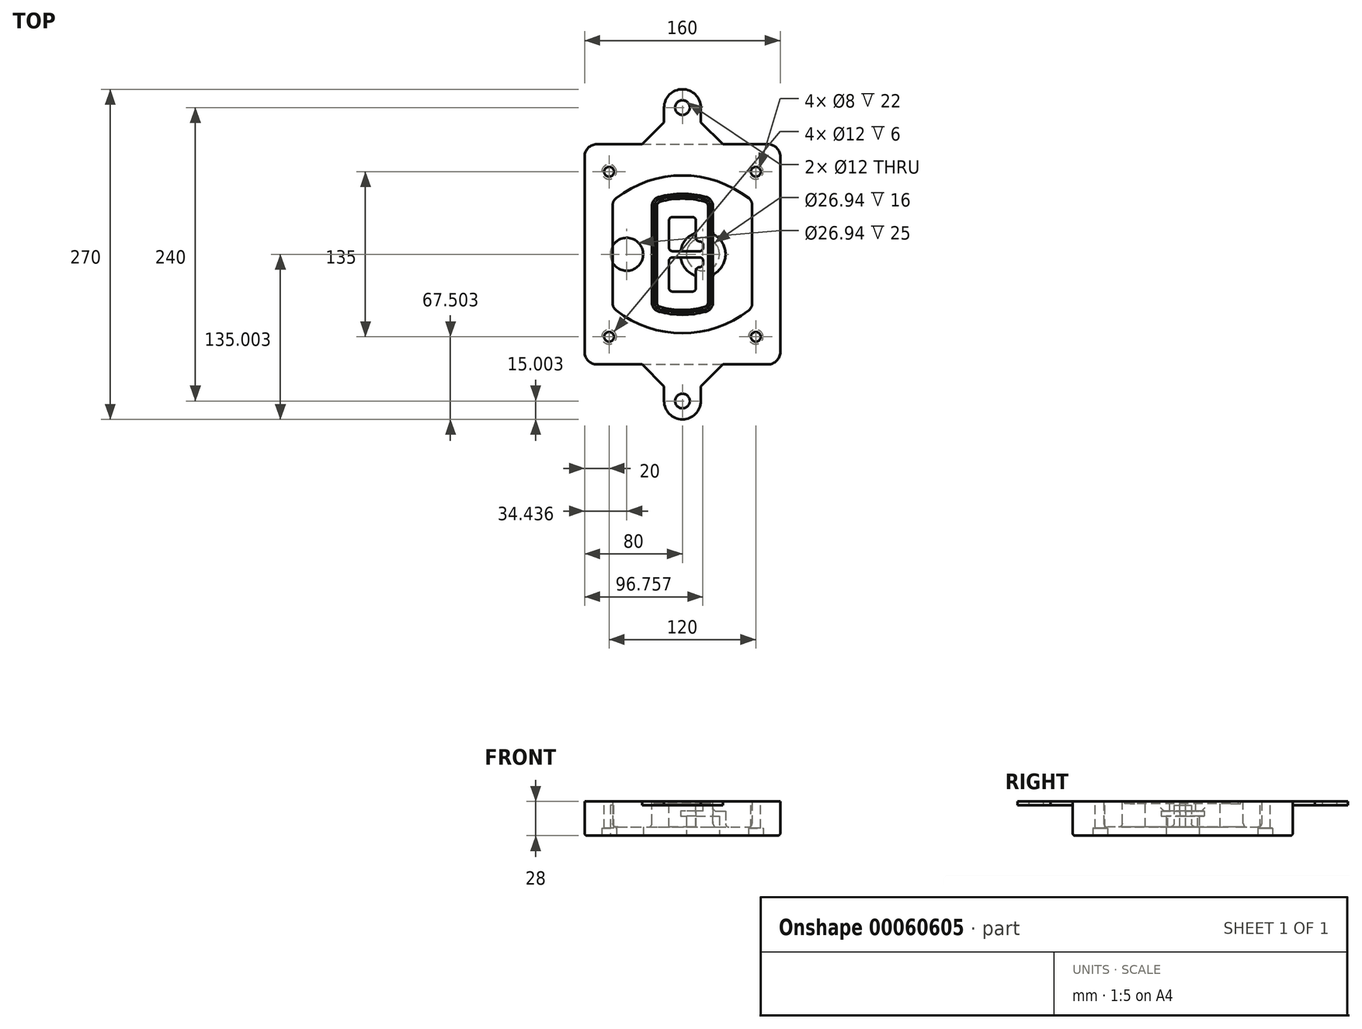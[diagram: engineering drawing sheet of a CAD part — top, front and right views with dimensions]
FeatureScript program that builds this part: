
annotation { "Feature Type Name" : "Feature", "Feature Type Description" : "" }
export const myFeature = defineFeature(function(context is Context, id is Id, definition is map)
    precondition{}
    {
        {
            var Q0;
            Q0=qCreatedBy(makeId("Top.planeOp"),FACE);
            var sketch = newSketch(context, id + "F0", { "sketchPlane" : qUnion([Q0])});
            skPoint(sketch, "E0.rect.middle", {"position": v(0, 0) * mm});
            skLineSegment(sketch, "E1.bottom", {"start": v(24.05, 28.38) * mm, "end": v(164.05, 28.38) * mm});
            skLineSegment(sketch, "E1.top", {"start": v(24.05, 208.38) * mm, "end": v(164.05, 208.38) * mm});
            skLineSegment(sketch, "E1.left", {"start": v(14.05, 38.38) * mm, "end": v(14.05, 198.38) * mm});
            skLineSegment(sketch, "E1.right", {"start": v(174.05, 38.38) * mm, "end": v(174.05, 198.38) * mm});
            skLineSegment(sketch, "E2", {"start": v(14.05, 208.38) * mm, "end": v(174.05, 28.38) * mm, "construction": true});
            skLineSegment(sketch, "E3", {"start": v(174.05, 208.38) * mm, "end": v(14.05, 28.38) * mm, "construction": true});
            skCircle(sketch, "E4", {"center": v(34.05, 185.88) * mm, "radius": 4 * mm});
            skCircle(sketch, "E5", {"center": v(154.05, 185.88) * mm, "radius": 4 * mm});
            skCircle(sketch, "E6", {"center": v(154.05, 50.88) * mm, "radius": 4 * mm});
            skCircle(sketch, "E7", {"center": v(34.05, 50.88) * mm, "radius": 4 * mm});
            skLineSegment(sketch, "E8", {"start": v(34.05, 185.88) * mm, "end": v(154.05, 185.88) * mm, "construction": true});
            skLineSegment(sketch, "E9", {"start": v(154.05, 185.88) * mm, "end": v(154.05, 50.88) * mm, "construction": true});
            skLineSegment(sketch, "E10", {"start": v(154.05, 50.88) * mm, "end": v(34.05, 50.88) * mm, "construction": true});
            skLineSegment(sketch, "E11", {"start": v(34.05, 50.88) * mm, "end": v(34.05, 185.88) * mm, "construction": true});
            skLineSegment(sketch, "E12", {"start": v(34.05, 158.68) * mm, "end": v(34.05, 78.09) * mm});
            skLineSegment(sketch, "E13", {"start": v(154.05, 158.68) * mm, "end": v(154.05, 78.09) * mm});
            skArc(sketch, "E14", {"start": v(150.2, 166.56) * mm, "mid": v(94.05, 185.88) * mm, "end": v(37.9, 166.56) * mm});
            skArc(sketch, "E15", {"start": v(37.9, 70.2) * mm, "mid": v(94.05, 50.88) * mm, "end": v(150.2, 70.2) * mm});
            skLineSegment(sketch, "E16", {"start": v(34.05, 118.38) * mm, "end": v(154.05, 118.38) * mm, "construction": true});
            skPoint(sketch, "E17.visualSharp", {"position": v(34.05, 73.38) * mm});
            skArc(sketch, "E17.filletArc", {"start": v(34.05, 78.09) * mm, "mid": v(35.06, 73.7) * mm, "end": v(37.9, 70.2) * mm});
            skPoint(sketch, "E18.visualSharp", {"position": v(34.05, 163.38) * mm});
            skArc(sketch, "E18.filletArc", {"start": v(37.9, 166.56) * mm, "mid": v(35.06, 163.06) * mm, "end": v(34.05, 158.68) * mm});
            skPoint(sketch, "E19.visualSharp", {"position": v(154.05, 163.38) * mm});
            skArc(sketch, "E19.filletArc", {"start": v(154.05, 158.68) * mm, "mid": v(153.04, 163.06) * mm, "end": v(150.2, 166.56) * mm});
            skPoint(sketch, "E20.visualSharp", {"position": v(154.05, 73.38) * mm});
            skArc(sketch, "E20.filletArc", {"start": v(150.2, 70.2) * mm, "mid": v(153.04, 73.7) * mm, "end": v(154.05, 78.09) * mm});
            skPoint(sketch, "E21.visualSharp", {"position": v(14.05, 208.38) * mm});
            skArc(sketch, "E21.filletArc", {"start": v(24.05, 208.38) * mm, "mid": v(16.98, 205.45) * mm, "end": v(14.05, 198.38) * mm});
            skPoint(sketch, "E22.visualSharp", {"position": v(174.05, 208.38) * mm});
            skArc(sketch, "E22.filletArc", {"start": v(174.05, 198.38) * mm, "mid": v(171.12, 205.45) * mm, "end": v(164.05, 208.38) * mm});
            skPoint(sketch, "E23.visualSharp", {"position": v(174.05, 28.38) * mm});
            skArc(sketch, "E23.filletArc", {"start": v(164.05, 28.38) * mm, "mid": v(171.12, 31.31) * mm, "end": v(174.05, 38.38) * mm});
            skPoint(sketch, "E24.visualSharp", {"position": v(14.05, 28.38) * mm});
            skArc(sketch, "E24.filletArc", {"start": v(14.05, 38.38) * mm, "mid": v(16.98, 31.31) * mm, "end": v(24.05, 28.38) * mm});
            skArc(sketch, "E25.0", {"start": v(151.05, 158.68) * mm, "mid": v(150.34, 161.75) * mm, "end": v(148.36, 164.2) * mm});
            skLineSegment(sketch, "E25.1", {"start": v(151.05, 158.68) * mm, "end": v(151.05, 78.09) * mm});
            skArc(sketch, "E25.2", {"start": v(148.36, 72.57) * mm, "mid": v(150.34, 75.02) * mm, "end": v(151.05, 78.09) * mm});
            skArc(sketch, "E25.3", {"start": v(39.74, 72.57) * mm, "mid": v(94.05, 53.88) * mm, "end": v(148.36, 72.57) * mm});
            skArc(sketch, "E25.4", {"start": v(37.05, 78.09) * mm, "mid": v(37.76, 75.02) * mm, "end": v(39.74, 72.57) * mm});
            skArc(sketch, "E25.5", {"start": v(148.36, 164.2) * mm, "mid": v(94.05, 182.88) * mm, "end": v(39.74, 164.2) * mm});
            skLineSegment(sketch, "E25.6", {"start": v(37.05, 158.68) * mm, "end": v(37.05, 78.09) * mm});
            skArc(sketch, "E25.7", {"start": v(39.74, 164.2) * mm, "mid": v(37.76, 161.75) * mm, "end": v(37.05, 158.68) * mm});
            skArc(sketch, "E26.0", {"start": v(35.43, 169.71) * mm, "mid": v(31.47, 164.82) * mm, "end": v(30.05, 158.68) * mm});
            skArc(sketch, "E26.1", {"start": v(152.67, 169.71) * mm, "mid": v(94.05, 189.88) * mm, "end": v(35.43, 169.71) * mm});
            skArc(sketch, "E26.2", {"start": v(158.05, 158.68) * mm, "mid": v(156.63, 164.82) * mm, "end": v(152.67, 169.71) * mm});
            skLineSegment(sketch, "E26.3", {"start": v(158.05, 158.68) * mm, "end": v(158.05, 78.09) * mm});
            skArc(sketch, "E26.4", {"start": v(152.67, 67.05) * mm, "mid": v(156.63, 71.95) * mm, "end": v(158.05, 78.09) * mm});
            skLineSegment(sketch, "E26.5", {"start": v(30.05, 158.68) * mm, "end": v(30.05, 78.09) * mm});
            skArc(sketch, "E26.6", {"start": v(35.43, 67.05) * mm, "mid": v(94.05, 46.88) * mm, "end": v(152.67, 67.05) * mm});
            skArc(sketch, "E26.7", {"start": v(30.05, 78.09) * mm, "mid": v(31.47, 71.95) * mm, "end": v(35.43, 67.05) * mm});
            skSolve(sketch);
        }
        {
            var Q0;
            Q0=makeQuery(id+"F0.imprint","IMPRINT",FACE,{"disambiguationData":[TD([[makeQuery(id+"F0.imprint","IMPRINT",EDGE,{"derivedFrom":sQuery(id+"F0.wireOp",EDGE,"E1.bottom")}),1.0]])]});
            var Q1;
            Q1=makeQuery(id+"F0.imprint","IMPRINT",FACE,{"disambiguationData":[TD([[makeQuery(id+"F0.imprint","IMPRINT",EDGE,{"derivedFrom":sQuery(id+"F0.wireOp",EDGE,"E12")}),1.0]])]});
            var Q2;
            Q2=makeQuery(id+"F0.imprint","IMPRINT",FACE,{"disambiguationData":[TD([[makeQuery(id+"F0.imprint","IMPRINT",EDGE,{"derivedFrom":sQuery(id+"F0.wireOp",EDGE,"E25.0")}),1.0]])]});
            var Q3;
            Q3=makeQuery(id+"F0.imprint","IMPRINT",FACE,{"disambiguationData":[TD([[makeQuery(id+"F0.imprint","IMPRINT",EDGE,{"derivedFrom":sQuery(id+"F0.wireOp",EDGE,"E12")}),-1.0]])]});
            extrude(context, id + "F1", {"entities" : qUnion([Q0, Q1, Q2, Q3]), "oppositeDirection" : true, "depth" : 25 * mm});
        }
        {
            var Q0;
            Q0=makeQuery(id+"F0.imprint","IMPRINT",FACE,{"disambiguationData":[TD([[makeQuery(id+"F0.imprint","IMPRINT",EDGE,{"derivedFrom":sQuery(id+"F0.wireOp",EDGE,"E12")}),1.0]])]});
            extrude(context, id + "F2", {"entities" : qUnion([Q0]), "operationType" : NewBodyOperationType.ADD, "depth" : 3 * mm});
        }
        {
            var Q0;
            Q0=makeQuery(id+"F0.imprint","IMPRINT",FACE,{"disambiguationData":[TD([[makeQuery(id+"F0.imprint","IMPRINT",EDGE,{"derivedFrom":sQuery(id+"F0.wireOp",EDGE,"E25.0")}),1.0]])]});
            extrude(context, id + "F3", {"entities" : qUnion([Q0]), "operationType" : NewBodyOperationType.REMOVE, "oppositeDirection" : true, "depth" : 18 * mm});
        }
        {
            var Q0;
            Q0=makeQuery(id+"F2.opExtrude","CAP_FACE",FACE,{"disambiguationData":[OSD([sQuery(id+"F0.wireOp",EDGE,"E12"),sQuery(id+"F0.wireOp",EDGE,"E13"),sQuery(id+"F0.wireOp",EDGE,"E14"),sQuery(id+"F0.wireOp",EDGE,"E15"),sQuery(id+"F0.wireOp",EDGE,"E17.filletArc"),sQuery(id+"F0.wireOp",EDGE,"E18.filletArc"),sQuery(id+"F0.wireOp",EDGE,"E19.filletArc"),sQuery(id+"F0.wireOp",EDGE,"E20.filletArc"),sQuery(id+"F0.wireOp",EDGE,"E25.0"),sQuery(id+"F0.wireOp",EDGE,"E25.1"),sQuery(id+"F0.wireOp",EDGE,"E25.2"),sQuery(id+"F0.wireOp",EDGE,"E25.3"),sQuery(id+"F0.wireOp",EDGE,"E25.4"),sQuery(id+"F0.wireOp",EDGE,"E25.5"),sQuery(id+"F0.wireOp",EDGE,"E25.6"),sQuery(id+"F0.wireOp",EDGE,"E25.7")])],"isStart":false});
            var sketch = newSketch(context, id + "F4", { "sketchPlane" : qUnion([Q0])});
            skArc(sketch, "E27.0", {"start": v(74.97, 71.41) * mm, "mid": v(94.05, 68.88) * mm, "end": v(113.13, 71.41) * mm});
            skArc(sketch, "E28.0", {"start": v(113.13, 165.35) * mm, "mid": v(94.05, 167.88) * mm, "end": v(74.97, 165.35) * mm});
            skLineSegment(sketch, "E29", {"start": v(69.05, 157.63) * mm, "end": v(69.05, 79.14) * mm});
            skLineSegment(sketch, "E30", {"start": v(119.05, 157.63) * mm, "end": v(119.05, 79.14) * mm});
            skLineSegment(sketch, "E31", {"start": v(69.05, 163.48) * mm, "end": v(119.05, 163.48) * mm, "construction": true});
            skLineSegment(sketch, "E32", {"start": v(69.05, 73.28) * mm, "end": v(119.05, 73.28) * mm, "construction": true});
            skPoint(sketch, "E33.visualSharp", {"position": v(69.05, 163.48) * mm});
            skArc(sketch, "E33.filletArc", {"start": v(74.97, 165.35) * mm, "mid": v(70.7, 162.5) * mm, "end": v(69.05, 157.63) * mm});
            skPoint(sketch, "E34.visualSharp", {"position": v(119.05, 163.48) * mm});
            skArc(sketch, "E34.filletArc", {"start": v(119.05, 157.63) * mm, "mid": v(117.4, 162.5) * mm, "end": v(113.13, 165.35) * mm});
            skPoint(sketch, "E35.visualSharp", {"position": v(119.05, 73.28) * mm});
            skArc(sketch, "E35.filletArc", {"start": v(113.13, 71.41) * mm, "mid": v(117.4, 74.27) * mm, "end": v(119.05, 79.14) * mm});
            skPoint(sketch, "E36.visualSharp", {"position": v(69.05, 73.28) * mm});
            skArc(sketch, "E36.filletArc", {"start": v(69.05, 79.14) * mm, "mid": v(70.7, 74.27) * mm, "end": v(74.97, 71.41) * mm});
            skArc(sketch, "E37.0", {"start": v(148.36, 164.2) * mm, "mid": v(94.05, 182.88) * mm, "end": v(39.74, 164.2) * mm});
            skArc(sketch, "E37.1", {"start": v(39.74, 164.2) * mm, "mid": v(37.76, 161.75) * mm, "end": v(37.05, 158.68) * mm});
            skLineSegment(sketch, "E37.2", {"start": v(37.05, 158.68) * mm, "end": v(37.05, 78.09) * mm});
            skArc(sketch, "E37.3", {"start": v(37.05, 78.09) * mm, "mid": v(37.76, 75.02) * mm, "end": v(39.74, 72.57) * mm});
            skArc(sketch, "E37.4", {"start": v(39.74, 72.57) * mm, "mid": v(94.05, 53.88) * mm, "end": v(148.36, 72.57) * mm});
            skArc(sketch, "E37.5", {"start": v(148.36, 72.57) * mm, "mid": v(150.34, 75.02) * mm, "end": v(151.05, 78.09) * mm});
            skLineSegment(sketch, "E37.6", {"start": v(151.05, 158.68) * mm, "end": v(151.05, 78.09) * mm});
            skArc(sketch, "E37.7", {"start": v(151.05, 158.68) * mm, "mid": v(150.34, 161.75) * mm, "end": v(148.36, 164.2) * mm});
            skLineSegment(sketch, "E38.0", {"start": v(117.05, 157.63) * mm, "end": v(117.05, 79.14) * mm});
            skArc(sketch, "E38.1", {"start": v(112.61, 73.34) * mm, "mid": v(115.81, 75.49) * mm, "end": v(117.05, 79.14) * mm});
            skArc(sketch, "E38.2", {"start": v(75.49, 73.34) * mm, "mid": v(94.05, 70.88) * mm, "end": v(112.61, 73.34) * mm});
            skArc(sketch, "E38.3", {"start": v(71.05, 79.14) * mm, "mid": v(72.29, 75.49) * mm, "end": v(75.49, 73.34) * mm});
            skLineSegment(sketch, "E38.4", {"start": v(71.05, 157.63) * mm, "end": v(71.05, 79.14) * mm});
            skArc(sketch, "E38.5", {"start": v(117.05, 157.63) * mm, "mid": v(115.81, 161.28) * mm, "end": v(112.61, 163.42) * mm});
            skArc(sketch, "E38.6", {"start": v(75.49, 163.42) * mm, "mid": v(72.29, 161.28) * mm, "end": v(71.05, 157.63) * mm});
            skArc(sketch, "E38.7", {"start": v(112.61, 163.42) * mm, "mid": v(94.05, 165.88) * mm, "end": v(75.49, 163.42) * mm});
            skArc(sketch, "E39.0", {"start": v(115.05, 157.63) * mm, "mid": v(114.23, 160.06) * mm, "end": v(112.1, 161.5) * mm});
            skLineSegment(sketch, "E39.1", {"start": v(115.05, 157.63) * mm, "end": v(115.05, 79.14) * mm});
            skArc(sketch, "E39.2", {"start": v(112.1, 75.27) * mm, "mid": v(114.23, 76.7) * mm, "end": v(115.05, 79.14) * mm});
            skArc(sketch, "E39.3", {"start": v(76, 75.27) * mm, "mid": v(94.05, 72.88) * mm, "end": v(112.1, 75.27) * mm});
            skArc(sketch, "E39.4", {"start": v(73.05, 79.14) * mm, "mid": v(73.87, 76.7) * mm, "end": v(76, 75.27) * mm});
            skArc(sketch, "E39.5", {"start": v(112.1, 161.5) * mm, "mid": v(94.05, 163.88) * mm, "end": v(76, 161.5) * mm});
            skLineSegment(sketch, "E39.6", {"start": v(73.05, 157.63) * mm, "end": v(73.05, 79.14) * mm});
            skArc(sketch, "E39.7", {"start": v(76, 161.5) * mm, "mid": v(73.87, 160.06) * mm, "end": v(73.05, 157.63) * mm});
            skLineSegment(sketch, "E40", {"start": v(69.05, 118.38) * mm, "end": v(119.05, 118.38) * mm, "construction": true});
            skLineSegment(sketch, "E41", {"start": v(83.05, 123.88) * mm, "end": v(83.05, 145.88) * mm});
            skLineSegment(sketch, "E42", {"start": v(86.05, 148.88) * mm, "end": v(102.05, 148.88) * mm});
            skLineSegment(sketch, "E43", {"start": v(105.05, 145.88) * mm, "end": v(105.05, 131.88) * mm});
            skLineSegment(sketch, "E44", {"start": v(108.05, 128.88) * mm, "end": v(108.05, 128.88) * mm});
            skLineSegment(sketch, "E45", {"start": v(111.05, 125.88) * mm, "end": v(111.05, 123.88) * mm});
            skLineSegment(sketch, "E46", {"start": v(108.05, 120.88) * mm, "end": v(86.05, 120.88) * mm});
            skPoint(sketch, "E47.visualSharp", {"position": v(83.05, 148.88) * mm});
            skArc(sketch, "E47.filletArc", {"start": v(86.05, 148.88) * mm, "mid": v(83.93, 148) * mm, "end": v(83.05, 145.88) * mm});
            skPoint(sketch, "E48.visualSharp", {"position": v(105.05, 148.88) * mm});
            skArc(sketch, "E48.filletArc", {"start": v(105.05, 145.88) * mm, "mid": v(104.17, 148) * mm, "end": v(102.05, 148.88) * mm});
            skPoint(sketch, "E49.visualSharp", {"position": v(105.05, 128.88) * mm});
            skArc(sketch, "E49.filletArc", {"start": v(105.05, 131.88) * mm, "mid": v(105.93, 129.76) * mm, "end": v(108.05, 128.88) * mm});
            skPoint(sketch, "E50.visualSharp", {"position": v(111.05, 128.88) * mm});
            skArc(sketch, "E50.filletArc", {"start": v(111.05, 125.88) * mm, "mid": v(110.17, 128) * mm, "end": v(108.05, 128.88) * mm});
            skPoint(sketch, "E51.visualSharp", {"position": v(111.05, 120.88) * mm});
            skArc(sketch, "E51.filletArc", {"start": v(108.05, 120.88) * mm, "mid": v(110.17, 121.76) * mm, "end": v(111.05, 123.88) * mm});
            skPoint(sketch, "E52.visualSharp", {"position": v(83.05, 120.88) * mm});
            skArc(sketch, "E52.filletArc", {"start": v(83.05, 123.88) * mm, "mid": v(83.93, 121.76) * mm, "end": v(86.05, 120.88) * mm});
            skLineSegment(sketch, "E53.0.MirrorCS", {"start": v(108.05, 115.88) * mm, "end": v(86.05, 115.88) * mm});
            skArc(sketch, "E54.0.MirrorCS", {"start": v(83.05, 112.88) * mm, "mid": v(83.93, 115) * mm, "end": v(86.05, 115.88) * mm});
            skLineSegment(sketch, "E55.0.MirrorCS", {"start": v(83.05, 112.88) * mm, "end": v(83.05, 90.88) * mm});
            skArc(sketch, "E56.0.MirrorCS", {"start": v(86.05, 87.88) * mm, "mid": v(83.93, 88.76) * mm, "end": v(83.05, 90.88) * mm});
            skLineSegment(sketch, "E57.0.MirrorCS", {"start": v(86.05, 87.88) * mm, "end": v(102.05, 87.88) * mm});
            skArc(sketch, "E58.0.MirrorCS", {"start": v(105.05, 90.88) * mm, "mid": v(104.17, 88.76) * mm, "end": v(102.05, 87.88) * mm});
            skLineSegment(sketch, "E59.0.MirrorCS", {"start": v(105.05, 90.88) * mm, "end": v(105.05, 104.88) * mm});
            skArc(sketch, "E60.0.MirrorCS", {"start": v(105.05, 104.88) * mm, "mid": v(105.93, 107) * mm, "end": v(108.05, 107.88) * mm});
            skArc(sketch, "E61.0.MirrorCS", {"start": v(111.05, 110.88) * mm, "mid": v(110.17, 108.76) * mm, "end": v(108.05, 107.88) * mm});
            skLineSegment(sketch, "E62.0.MirrorCS", {"start": v(111.05, 110.88) * mm, "end": v(111.05, 112.88) * mm});
            skArc(sketch, "E63.0.MirrorCS", {"start": v(108.05, 115.88) * mm, "mid": v(110.17, 115) * mm, "end": v(111.05, 112.88) * mm});
            skSolve(sketch);
        }
        {
            var Q0;
            Q0=makeQuery(id+"F4.imprint","IMPRINT",FACE,{"disambiguationData":[TD([[makeQuery(id+"F4.imprint","IMPRINT",EDGE,{"derivedFrom":sQuery(id+"F4.wireOp",EDGE,"E27.0")}),1.0]])]});
            var Q1;
            Q1=makeQuery(id+"F4.imprint","IMPRINT",FACE,{"disambiguationData":[TD([[makeQuery(id+"F4.imprint","IMPRINT",EDGE,{"derivedFrom":sQuery(id+"F4.wireOp",EDGE,"E38.0")}),-1.0]])]});
            var Q2;
            Q2=makeQuery(id+"F4.imprint","IMPRINT",FACE,{"disambiguationData":[TD([[makeQuery(id+"F4.imprint","IMPRINT",EDGE,{"derivedFrom":sQuery(id+"F4.wireOp",EDGE,"E39.0")}),1.0]])]});
            extrude(context, id + "F5", {"entities" : qUnion([Q0, Q1, Q2]), "operationType" : NewBodyOperationType.ADD, "endBound" : BoundingType.UP_TO_NEXT, "oppositeDirection" : true, "depth" : 25 * mm});
        }
        {
            var Q0;
            Q0=makeQuery(id+"F4.imprint","IMPRINT",FACE,{"disambiguationData":[TD([[makeQuery(id+"F4.imprint","IMPRINT",EDGE,{"derivedFrom":sQuery(id+"F4.wireOp",EDGE,"E38.0")}),-1.0]])]});
            extrude(context, id + "F6", {"entities" : qUnion([Q0]), "operationType" : NewBodyOperationType.REMOVE, "oppositeDirection" : true, "depth" : 2 * mm});
        }
        {
            var Q0;
            Q0=makeQuery(id+"F1.opExtrude","CAP_FACE",FACE,{"disambiguationData":[OSD([sQuery(id+"F0.wireOp",EDGE,"E1.bottom"),sQuery(id+"F0.wireOp",EDGE,"E1.top"),sQuery(id+"F0.wireOp",EDGE,"E1.left"),sQuery(id+"F0.wireOp",EDGE,"E1.right"),sQuery(id+"F0.wireOp",EDGE,"E4"),sQuery(id+"F0.wireOp",EDGE,"E5"),sQuery(id+"F0.wireOp",EDGE,"E6"),sQuery(id+"F0.wireOp",EDGE,"E7"),sQuery(id+"F0.wireOp",EDGE,"E21.filletArc"),sQuery(id+"F0.wireOp",EDGE,"E22.filletArc"),sQuery(id+"F0.wireOp",EDGE,"E23.filletArc"),sQuery(id+"F0.wireOp",EDGE,"E24.filletArc")])],"isStart":false});
            var sketch = newSketch(context, id + "F7", { "sketchPlane" : qUnion([Q0])});
            skCircle(sketch, "E64", {"center": v(110.8, -118.38) * mm, "radius": 13.47 * mm});
            skCircle(sketch, "E65", {"center": v(48.49, -118.38) * mm, "radius": 13.47 * mm});
            skLineSegment(sketch, "E66", {"start": v(174.05, -118.38) * mm, "end": v(14.05, -118.38) * mm});
            skCircle(sketch, "E67", {"center": v(110.8, -118.38) * mm, "radius": 18.47 * mm});
            skCircle(sketch, "E68", {"center": v(154.05, -185.88) * mm, "radius": 6 * mm});
            skCircle(sketch, "E69", {"center": v(34.05, -185.88) * mm, "radius": 6 * mm});
            skCircle(sketch, "E70", {"center": v(34.05, -50.88) * mm, "radius": 6 * mm});
            skCircle(sketch, "E71", {"center": v(154.05, -50.88) * mm, "radius": 6 * mm});
            skSolve(sketch);
        }
        {
            var Q0;
            {var subQ1=sQuery(id+"F7.wireOp",EDGE,"E66");var subQ4=sQuery(id+"F7.wireOp",EDGE,"E64");var subQ6=makeQuery(id+"F7.imprint","INTERSECT",VERTEX,{"disambiguationData":[OD(0.0)],"derivedFrom":[subQ4,subQ1]});Q0=makeQuery(id+"F7.imprint","IMPRINT",FACE,{"disambiguationData":[TD([[makeQuery(id+"F7.imprint","IMPRINT",EDGE,{"disambiguationData":[TD([[subQ6,-1.0]])],"derivedFrom":subQ4}),-1.0]])]});}
            var Q1;
            {var subQ0=sQuery(id+"F7.wireOp",EDGE,"E66");var subQ1=sQuery(id+"F7.wireOp",EDGE,"E64");var subQ3=makeQuery(id+"F7.imprint","INTERSECT",VERTEX,{"disambiguationData":[OD(0.0)],"derivedFrom":[subQ1,subQ0]});Q1=makeQuery(id+"F7.imprint","IMPRINT",FACE,{"disambiguationData":[TD([[makeQuery(id+"F7.imprint","IMPRINT",EDGE,{"disambiguationData":[TD([[subQ3,-1.0]])],"derivedFrom":subQ1}),1.0]])]});}
            var Q2;
            {var subQ0=sQuery(id+"F7.wireOp",EDGE,"E66");var subQ1=sQuery(id+"F7.wireOp",EDGE,"E64");var subQ3=makeQuery(id+"F7.imprint","INTERSECT",VERTEX,{"disambiguationData":[OD(0.0)],"derivedFrom":[subQ1,subQ0]});Q2=makeQuery(id+"F7.imprint","IMPRINT",FACE,{"disambiguationData":[TD([[makeQuery(id+"F7.imprint","IMPRINT",EDGE,{"disambiguationData":[TD([[subQ3,1.0]])],"derivedFrom":subQ1}),1.0]])]});}
            var Q3;
            {var subQ1=sQuery(id+"F7.wireOp",EDGE,"E66");var subQ4=sQuery(id+"F7.wireOp",EDGE,"E64");var subQ6=makeQuery(id+"F7.imprint","INTERSECT",VERTEX,{"disambiguationData":[OD(0.0)],"derivedFrom":[subQ4,subQ1]});Q3=makeQuery(id+"F7.imprint","IMPRINT",FACE,{"disambiguationData":[TD([[makeQuery(id+"F7.imprint","IMPRINT",EDGE,{"disambiguationData":[TD([[subQ6,1.0]])],"derivedFrom":subQ4}),-1.0]])]});}
            extrude(context, id + "F8", {"entities" : qUnion([Q0, Q1, Q2, Q3]), "operationType" : NewBodyOperationType.ADD, "oppositeDirection" : true, "depth" : 20 * mm});
        }
        {
            var Q0;
            {var subQ0=sQuery(id+"F7.wireOp",EDGE,"E66");var subQ1=sQuery(id+"F7.wireOp",EDGE,"E64");var subQ3=makeQuery(id+"F7.imprint","INTERSECT",VERTEX,{"disambiguationData":[OD(0.0)],"derivedFrom":[subQ1,subQ0]});Q0=makeQuery(id+"F7.imprint","IMPRINT",FACE,{"disambiguationData":[TD([[makeQuery(id+"F7.imprint","IMPRINT",EDGE,{"disambiguationData":[TD([[subQ3,-1.0]])],"derivedFrom":subQ1}),1.0]])]});}
            var Q1;
            {var subQ0=sQuery(id+"F7.wireOp",EDGE,"E66");var subQ1=sQuery(id+"F7.wireOp",EDGE,"E64");var subQ3=makeQuery(id+"F7.imprint","INTERSECT",VERTEX,{"disambiguationData":[OD(0.0)],"derivedFrom":[subQ1,subQ0]});Q1=makeQuery(id+"F7.imprint","IMPRINT",FACE,{"disambiguationData":[TD([[makeQuery(id+"F7.imprint","IMPRINT",EDGE,{"disambiguationData":[TD([[subQ3,1.0]])],"derivedFrom":subQ1}),1.0]])]});}
            extrude(context, id + "F9", {"entities" : qUnion([Q0, Q1]), "operationType" : NewBodyOperationType.REMOVE, "oppositeDirection" : true, "depth" : 16 * mm});
        }
        {
            var Q0;
            {var subQ0=sQuery(id+"F7.wireOp",EDGE,"E66");var subQ1=sQuery(id+"F7.wireOp",EDGE,"E65");var subQ3=makeQuery(id+"F7.imprint","INTERSECT",VERTEX,{"disambiguationData":[OD(0.0)],"derivedFrom":[subQ1,subQ0]});Q0=makeQuery(id+"F7.imprint","IMPRINT",FACE,{"disambiguationData":[TD([[makeQuery(id+"F7.imprint","IMPRINT",EDGE,{"disambiguationData":[TD([[subQ3,-1.0]])],"derivedFrom":subQ1}),1.0]])]});}
            var Q1;
            {var subQ0=sQuery(id+"F7.wireOp",EDGE,"E66");var subQ1=sQuery(id+"F7.wireOp",EDGE,"E65");var subQ3=makeQuery(id+"F7.imprint","INTERSECT",VERTEX,{"disambiguationData":[OD(0.0)],"derivedFrom":[subQ1,subQ0]});Q1=makeQuery(id+"F7.imprint","IMPRINT",FACE,{"disambiguationData":[TD([[makeQuery(id+"F7.imprint","IMPRINT",EDGE,{"disambiguationData":[TD([[subQ3,1.0]])],"derivedFrom":subQ1}),1.0]])]});}
            extrude(context, id + "F10", {"entities" : qUnion([Q0, Q1]), "operationType" : NewBodyOperationType.REMOVE, "oppositeDirection" : true, "depth" : 25 * mm});
        }
        {
            var Q0;
            Q0=makeQuery(id+"F7.imprint","IMPRINT",FACE,{"disambiguationData":[TD([[makeQuery(id+"F7.imprint","IMPRINT",EDGE,{"derivedFrom":sQuery(id+"F7.wireOp",EDGE,"E68")}),1.0]])]});
            var Q1;
            Q1=makeQuery(id+"F7.imprint","IMPRINT",FACE,{"disambiguationData":[TD([[makeQuery(id+"F7.imprint","IMPRINT",EDGE,{"derivedFrom":makeQuery(id+"F1.opExtrude","CAP_EDGE",EDGE,{"disambiguationData":[OSD([sQuery(id+"F0.wireOp",EDGE,"E5")])],"isStart":false})}),-1.0]])]});
            var Q2;
            Q2=makeQuery(id+"F7.imprint","IMPRINT",FACE,{"disambiguationData":[TD([[makeQuery(id+"F7.imprint","IMPRINT",EDGE,{"derivedFrom":sQuery(id+"F7.wireOp",EDGE,"E69")}),1.0]])]});
            var Q3;
            Q3=makeQuery(id+"F7.imprint","IMPRINT",FACE,{"disambiguationData":[TD([[makeQuery(id+"F7.imprint","IMPRINT",EDGE,{"derivedFrom":makeQuery(id+"F1.opExtrude","CAP_EDGE",EDGE,{"disambiguationData":[OSD([sQuery(id+"F0.wireOp",EDGE,"E4")])],"isStart":false})}),-1.0]])]});
            var Q4;
            Q4=makeQuery(id+"F7.imprint","IMPRINT",FACE,{"disambiguationData":[TD([[makeQuery(id+"F7.imprint","IMPRINT",EDGE,{"derivedFrom":sQuery(id+"F7.wireOp",EDGE,"E70")}),1.0]])]});
            var Q5;
            Q5=makeQuery(id+"F7.imprint","IMPRINT",FACE,{"disambiguationData":[TD([[makeQuery(id+"F7.imprint","IMPRINT",EDGE,{"derivedFrom":makeQuery(id+"F1.opExtrude","CAP_EDGE",EDGE,{"disambiguationData":[OSD([sQuery(id+"F0.wireOp",EDGE,"E7")])],"isStart":false})}),-1.0]])]});
            var Q6;
            Q6=makeQuery(id+"F7.imprint","IMPRINT",FACE,{"disambiguationData":[TD([[makeQuery(id+"F7.imprint","IMPRINT",EDGE,{"derivedFrom":sQuery(id+"F7.wireOp",EDGE,"E71")}),1.0]])]});
            var Q7;
            Q7=makeQuery(id+"F7.imprint","IMPRINT",FACE,{"disambiguationData":[TD([[makeQuery(id+"F7.imprint","IMPRINT",EDGE,{"derivedFrom":makeQuery(id+"F1.opExtrude","CAP_EDGE",EDGE,{"disambiguationData":[OSD([sQuery(id+"F0.wireOp",EDGE,"E6")])],"isStart":false})}),-1.0]])]});
            extrude(context, id + "F11", {"entities" : qUnion([Q0, Q1, Q2, Q3, Q4, Q5, Q6, Q7]), "operationType" : NewBodyOperationType.REMOVE, "oppositeDirection" : true, "depth" : 6 * mm});
        }
        {
            var Q0;
            Q0=makeQuery(id+"F9.boolean.opBoolean","COPY",FACE,{"derivedFrom":makeQuery(id+"F9.opExtrude","CAP_FACE",FACE,{"disambiguationData":[OSD([sQuery(id+"F7.wireOp",EDGE,"E64")])],"isStart":false})});
            var sketch = newSketch(context, id + "F12", { "sketchPlane" : qUnion([Q0])});
            skArc(sketch, "E72.0", {"start": v(105.05, -100.83) * mm, "mid": v(96.62, -106.56) * mm, "end": v(92.5, -115.88) * mm});
            skArc(sketch, "E72.1", {"start": v(92.5, -120.88) * mm, "mid": v(96.62, -130.2) * mm, "end": v(105.05, -135.93) * mm});
            skLineSegment(sketch, "E73", {"start": v(92.5, -120.88) * mm, "end": v(108.05, -120.88) * mm});
            skLineSegment(sketch, "E74.0", {"start": v(108.05, -115.88) * mm, "end": v(92.5, -115.88) * mm});
            skArc(sketch, "E74.1", {"start": v(108.05, -115.88) * mm, "mid": v(110.17, -115) * mm, "end": v(111.05, -112.88) * mm});
            skLineSegment(sketch, "E74.2", {"start": v(111.05, -110.88) * mm, "end": v(111.05, -112.88) * mm});
            skArc(sketch, "E74.3", {"start": v(111.05, -110.88) * mm, "mid": v(110.17, -108.76) * mm, "end": v(108.05, -107.88) * mm});
            skArc(sketch, "E74.4", {"start": v(105.05, -104.88) * mm, "mid": v(105.93, -107) * mm, "end": v(108.05, -107.88) * mm});
            skLineSegment(sketch, "E74.5", {"start": v(105.05, -100.83) * mm, "end": v(105.05, -104.88) * mm});
            skLineSegment(sketch, "E74.7", {"start": v(108.05, -120.88) * mm, "end": v(92.5, -120.88) * mm});
            skArc(sketch, "E74.8", {"start": v(108.05, -120.88) * mm, "mid": v(110.17, -121.76) * mm, "end": v(111.05, -123.88) * mm});
            skLineSegment(sketch, "E74.9", {"start": v(111.05, -125.88) * mm, "end": v(111.05, -123.88) * mm});
            skArc(sketch, "E74.10", {"start": v(111.05, -125.88) * mm, "mid": v(110.17, -128) * mm, "end": v(108.05, -128.88) * mm});
            skArc(sketch, "E74.11", {"start": v(105.05, -131.88) * mm, "mid": v(105.93, -129.76) * mm, "end": v(108.05, -128.88) * mm});
            skLineSegment(sketch, "E74.12", {"start": v(105.05, -135.93) * mm, "end": v(105.05, -131.88) * mm});
            skPoint(sketch, "E75.orphan", {"position": v(105.05, -145.88) * mm});
            skPoint(sketch, "E76.orphan", {"position": v(86.05, -120.88) * mm});
            skPoint(sketch, "E77.orphan", {"position": v(86.05, -115.88) * mm});
            skPoint(sketch, "E78.orphan", {"position": v(105.05, -90.88) * mm});
            skSolve(sketch);
        }
        {
            var Q0;
            {var subQ7=sQuery(id+"F12.wireOp",EDGE,"E72.0");var subQ14=sQuery(id+"F12.wireOp",EDGE,"E72.1");var subQ16=sQuery(id+"F12.wireOp",EDGE,"E74.1");var subQ18=sQuery(id+"F12.wireOp",EDGE,"E74.8");Q0=qUnion([makeQuery(id+"F12.imprint","IMPRINT",FACE,{"disambiguationData":[TD([[makeQuery(id+"F12.imprint","IMPRINT",EDGE,{"derivedFrom":subQ7}),1.0]])]}),makeQuery(id+"F12.imprint","IMPRINT",FACE,{"disambiguationData":[TD([[makeQuery(id+"F12.imprint","IMPRINT",EDGE,{"derivedFrom":subQ14}),1.0]])]}),makeQuery(id+"F12.imprint","IMPRINT",FACE,{"disambiguationData":[TD([[makeQuery(id+"F12.imprint","IMPRINT",EDGE,{"derivedFrom":subQ16}),1.0]])]}),makeQuery(id+"F12.imprint","IMPRINT",FACE,{"disambiguationData":[TD([[makeQuery(id+"F12.imprint","IMPRINT",EDGE,{"derivedFrom":subQ18}),-1.0]])]})]);}
            var Q1;
            Q1=makeQuery(id+"F5.boolean.opBoolean","SPLIT",FACE,{"disambiguationData":[TD([makeQuery(id+"F5.opExtrude","SWEPT_FACE",FACE,{"disambiguationData":[OSD([sQuery(id+"F4.wireOp",EDGE,"E41")])]})])],"derivedFrom":makeQuery(id+"F3.boolean.opBoolean","COPY",FACE,{"derivedFrom":makeQuery(id+"F3.opExtrude","CAP_FACE",FACE,{"disambiguationData":[OSD([sQuery(id+"F0.wireOp",EDGE,"E25.0"),sQuery(id+"F0.wireOp",EDGE,"E25.1"),sQuery(id+"F0.wireOp",EDGE,"E25.2"),sQuery(id+"F0.wireOp",EDGE,"E25.3"),sQuery(id+"F0.wireOp",EDGE,"E25.4"),sQuery(id+"F0.wireOp",EDGE,"E25.5"),sQuery(id+"F0.wireOp",EDGE,"E25.6"),sQuery(id+"F0.wireOp",EDGE,"E25.7")])],"isStart":false})})});
            extrude(context, id + "F13", {"entities" : qUnion([Q0]), "operationType" : NewBodyOperationType.REMOVE, "endBound" : BoundingType.UP_TO_SURFACE, "endBoundEntityFace" : qUnion([Q1]), "depth" : 25 * mm});
        }
        {
            var Q0;
            Q0=makeQuery(id+"F3.boolean.opBoolean","COPY",EDGE,{"derivedFrom":makeQuery(id+"F3.opExtrude","CAP_EDGE",EDGE,{"disambiguationData":[OSD([sQuery(id+"F0.wireOp",EDGE,"E25.6")])],"isStart":false})});
            var Q1;
            Q1=makeQuery(id+"F8.boolean.opBoolean","INTERSECT",EDGE,{"derivedFrom":[makeQuery(id+"F5.opExtrude","SWEPT_FACE",FACE,{"disambiguationData":[OSD([sQuery(id+"F4.wireOp",EDGE,"E30")])]}),makeQuery(id+"F8.opExtrude","CAP_FACE",FACE,{"disambiguationData":[OSD([sQuery(id+"F7.wireOp",EDGE,"E67")])],"isStart":false})]});
            var Q2;
            Q2=makeQuery(id+"F8.boolean.opBoolean","INTERSECT",EDGE,{"disambiguationData":[OD(1.0)],"derivedFrom":[makeQuery(id+"F5.opExtrude","SWEPT_FACE",FACE,{"disambiguationData":[OSD([sQuery(id+"F4.wireOp",EDGE,"E30")])]}),makeQuery(id+"F8.opExtrude","SWEPT_FACE",FACE,{"disambiguationData":[OSD([sQuery(id+"F7.wireOp",EDGE,"E67")])]})]});
            var Q3;
            {var subQ0=sQuery(id+"F4.wireOp",EDGE,"E30");Q3=makeQuery(id+"F8.boolean.opBoolean","SPLIT",EDGE,{"disambiguationData":[TD([makeQuery(id+"F5.opExtrude","SWEPT_FACE",FACE,{"disambiguationData":[OSD([sQuery(id+"F4.wireOp",EDGE,"E35.filletArc")])]})])],"derivedFrom":makeQuery(id+"F5.opExtrude","CAP_EDGE",EDGE,{"disambiguationData":[OSD([subQ0])],"isStart":false})});}
            var Q4;
            {var subQ0=sQuery(id+"F0.wireOp",EDGE,"E25.7");var subQ1=sQuery(id+"F0.wireOp",EDGE,"E25.1");var subQ2=sQuery(id+"F0.wireOp",EDGE,"E25.6");var subQ3=sQuery(id+"F0.wireOp",EDGE,"E25.5");var subQ4=sQuery(id+"F0.wireOp",EDGE,"E25.4");var subQ5=sQuery(id+"F0.wireOp",EDGE,"E25.0");var subQ6=sQuery(id+"F0.wireOp",EDGE,"E25.2");var subQ7=sQuery(id+"F0.wireOp",EDGE,"E25.3");Q4=makeQuery(id+"F8.boolean.opBoolean","INTERSECT",EDGE,{"derivedFrom":[makeQuery(id+"F5.boolean.opBoolean","SPLIT",FACE,{"disambiguationData":[TD([makeQuery(id+"F2.opExtrude","SWEPT_FACE",FACE,{"disambiguationData":[OSD([subQ5])]})])],"derivedFrom":makeQuery(id+"F3.boolean.opBoolean","COPY",FACE,{"derivedFrom":makeQuery(id+"F3.opExtrude","CAP_FACE",FACE,{"disambiguationData":[OSD([subQ5,subQ1,subQ6,subQ7,subQ4,subQ3,subQ2,subQ0])],"isStart":false})})}),makeQuery(id+"F8.opExtrude","SWEPT_FACE",FACE,{"disambiguationData":[OSD([sQuery(id+"F7.wireOp",EDGE,"E67")])]})]});}
            var Q5;
            Q5=makeQuery(id+"F8.boolean.opBoolean","INTERSECT",EDGE,{"disambiguationData":[OD(0.0)],"derivedFrom":[makeQuery(id+"F5.opExtrude","SWEPT_FACE",FACE,{"disambiguationData":[OSD([sQuery(id+"F4.wireOp",EDGE,"E30")])]}),makeQuery(id+"F8.opExtrude","SWEPT_FACE",FACE,{"disambiguationData":[OSD([sQuery(id+"F7.wireOp",EDGE,"E67")])]})]});
            fillet(context, id + "F14", {"entities" : qUnion([Q0, Q1, Q2, Q3, Q4, Q5]), "radius" : 3 * mm, "tangentPropagation" : true, "allowEdgeOverflow" : false});
        }
        {
            var Q0;
            Q0=makeQuery(id+"F1.opExtrude","CAP_EDGE",EDGE,{"disambiguationData":[OSD([sQuery(id+"F0.wireOp",EDGE,"E1.bottom")])],"isStart":false});
            fillet(context, id + "F15", {"entities" : qUnion([Q0]), "radius" : 2 * mm, "tangentPropagation" : true, "allowEdgeOverflow" : false});
        }
        {
            var Q0;
            {var subQ0=sQuery(id+"F0.wireOp",EDGE,"E22.filletArc");var subQ1=sQuery(id+"F0.wireOp",EDGE,"E7");var subQ2=sQuery(id+"F0.wireOp",EDGE,"E6");var subQ3=sQuery(id+"F0.wireOp",EDGE,"E5");var subQ4=sQuery(id+"F0.wireOp",EDGE,"E4");var subQ5=sQuery(id+"F0.wireOp",EDGE,"E1.bottom");var subQ6=sQuery(id+"F0.wireOp",EDGE,"E21.filletArc");var subQ7=sQuery(id+"F0.wireOp",EDGE,"E1.top");var subQ8=sQuery(id+"F0.wireOp",EDGE,"E1.left");var subQ9=sQuery(id+"F0.wireOp",EDGE,"E1.right");var subQ10=sQuery(id+"F0.wireOp",EDGE,"E23.filletArc");var subQ11=sQuery(id+"F0.wireOp",EDGE,"E24.filletArc");Q0=makeQuery(id+"F2.boolean.opBoolean","SPLIT",FACE,{"disambiguationData":[TD([makeQuery(id+"F1.opExtrude","SWEPT_FACE",FACE,{"disambiguationData":[OSD([subQ5])]})])],"derivedFrom":makeQuery(id+"F1.opExtrude","CAP_FACE",FACE,{"disambiguationData":[OSD([subQ5,subQ7,subQ8,subQ9,subQ4,subQ3,subQ2,subQ1,subQ6,subQ0,subQ10,subQ11])],"isStart":true})});}
            var sketch = newSketch(context, id + "F16", { "sketchPlane" : qUnion([Q0])});
            skLineSegment(sketch, "E79", {"start": v(61.05, 208.38) * mm, "end": v(79.05, 226.38) * mm});
            skLineSegment(sketch, "E80", {"start": v(79.05, 226.38) * mm, "end": v(79.05, 238.38) * mm});
            skCircle(sketch, "E81", {"center": v(94.05, 238.38) * mm, "radius": 6 * mm});
            skLineSegment(sketch, "E82", {"start": v(94.05, 238.38) * mm, "end": v(94.05, 208.38) * mm, "construction": true});
            skArc(sketch, "E83", {"start": v(109.05, 238.38) * mm, "mid": v(94.05, 253.38) * mm, "end": v(79.05, 238.38) * mm});
            skLineSegment(sketch, "E84", {"start": v(109.05, 238.38) * mm, "end": v(109.05, 226.38) * mm});
            skLineSegment(sketch, "E85", {"start": v(109.05, 226.38) * mm, "end": v(127.05, 208.38) * mm});
            skLineSegment(sketch, "E86", {"start": v(14.05, 118.38) * mm, "end": v(174.05, 118.38) * mm, "construction": true});
            skPoint(sketch, "E86.startSnap0", {"position": v(34.05, 118.38) * mm});
            skPoint(sketch, "E86.endSnap0", {"position": v(174.05, 118.38) * mm});
            skLineSegment(sketch, "E87.MirrorCS", {"start": v(109.05, -1.62) * mm, "end": v(109.05, 10.38) * mm});
            skLineSegment(sketch, "E88.MirrorCS", {"start": v(79.05, 10.38) * mm, "end": v(79.05, -1.62) * mm});
            skArc(sketch, "E89.MirrorCS", {"start": v(109.05, -1.62) * mm, "mid": v(94.05, -16.62) * mm, "end": v(79.05, -1.62) * mm});
            skCircle(sketch, "E90.MirrorC", {"center": v(94.05, -1.62) * mm, "radius": 6 * mm});
            skLineSegment(sketch, "E91.MirrorCS", {"start": v(94.05, -1.62) * mm, "end": v(94.05, 28.38) * mm, "construction": true});
            skLineSegment(sketch, "E92.MirrorCS", {"start": v(109.05, 10.38) * mm, "end": v(127.05, 28.38) * mm});
            skLineSegment(sketch, "E93.MirrorCS", {"start": v(61.05, 28.38) * mm, "end": v(79.05, 10.38) * mm});
            skPoint(sketch, "E94.startSnap0", {"position": v(94.05, 208.38) * mm});
            skPoint(sketch, "E94.endSnap0", {"position": v(94.05, 28.38) * mm});
            skSolve(sketch);
        }
        {
            var Q0;
            Q0=makeQuery(id+"F16.imprint","IMPRINT",FACE,{"disambiguationData":[TD([[makeQuery(id+"F16.imprint","IMPRINT",EDGE,{"derivedFrom":makeQuery(id+"F1.opExtrude","CAP_EDGE",EDGE,{"disambiguationData":[OSD([sQuery(id+"F0.wireOp",EDGE,"E1.left")])],"isStart":true})}),-1.0]])]});
            var Q1;
            {var subQ1=sQuery(id+"F16.wireOp",EDGE,"E79");Q1=makeQuery(id+"F16.imprint","IMPRINT",FACE,{"disambiguationData":[TD([[makeQuery(id+"F16.imprint","IMPRINT",EDGE,{"derivedFrom":subQ1}),-1.0]])]});}
            var Q2;
            Q2=makeQuery(id+"F16.imprint","IMPRINT",FACE,{"disambiguationData":[TD([[makeQuery(id+"F16.imprint","IMPRINT",EDGE,{"derivedFrom":sQuery(id+"F16.wireOp",EDGE,"E87.MirrorCS")}),1.0]])]});
            var Q3;
            Q3=makeQuery(id+"F2.opExtrude","CAP_FACE",FACE,{"disambiguationData":[OSD([sQuery(id+"F0.wireOp",EDGE,"E12"),sQuery(id+"F0.wireOp",EDGE,"E13"),sQuery(id+"F0.wireOp",EDGE,"E14"),sQuery(id+"F0.wireOp",EDGE,"E15"),sQuery(id+"F0.wireOp",EDGE,"E17.filletArc"),sQuery(id+"F0.wireOp",EDGE,"E18.filletArc"),sQuery(id+"F0.wireOp",EDGE,"E19.filletArc"),sQuery(id+"F0.wireOp",EDGE,"E20.filletArc"),sQuery(id+"F0.wireOp",EDGE,"E25.0"),sQuery(id+"F0.wireOp",EDGE,"E25.1"),sQuery(id+"F0.wireOp",EDGE,"E25.2"),sQuery(id+"F0.wireOp",EDGE,"E25.3"),sQuery(id+"F0.wireOp",EDGE,"E25.4"),sQuery(id+"F0.wireOp",EDGE,"E25.5"),sQuery(id+"F0.wireOp",EDGE,"E25.6"),sQuery(id+"F0.wireOp",EDGE,"E25.7")])],"isStart":false});
            extrude(context, id + "F17", {"entities" : qUnion([Q0, Q1, Q2]), "operationType" : NewBodyOperationType.ADD, "endBound" : BoundingType.UP_TO_SURFACE, "endBoundEntityFace" : qUnion([Q3]), "depth" : 25 * mm});
        }
    });
